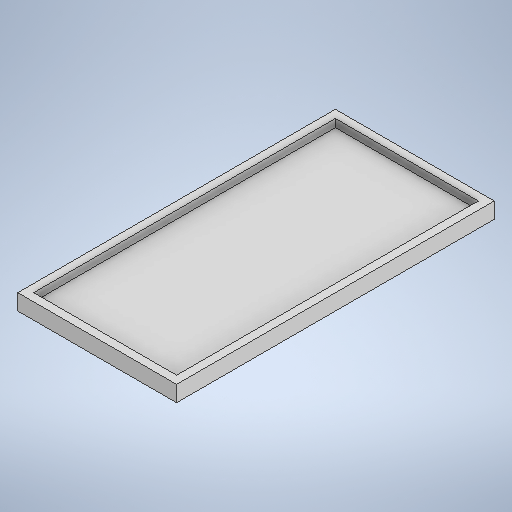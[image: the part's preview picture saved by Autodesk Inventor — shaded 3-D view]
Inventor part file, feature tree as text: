
AUTODESK INVENTOR PART (.ipt)
format: ipt  version: 2025 (Build 290162000, 162)  size: 242,688 bytes
history: native  units: in
note: dims shown in document units (in); Inventor stores cm internally (conversion verified against a paired STEP export)
features: extrude x2, sketch x1
ambient origin geometry x8: Origin, YZ Plane, XZ Plane, XY Plane, X Axis, Y Axis, Z Axis, Center Point
bodies: Solid1 (feature_tree)
feature tree (3):
  sketch  "Sketch1"  dims[d0=20.0in d1=10.0in d2=19.0in d3=9.0in d4=0.5in d5=0.0in d6=1.0in d7=0.0in]
  extrude  "Extrusion1"  Depth=10.0in
  extrude  "Extrusion2"  Depth=19.0in
